# Revit family: FU_Modular_Sandler_Tetris 8100PT
name_source: partatom
category: Furniture
units: mm (PartAtom-declared; Revit-internal decimal feet)

## family parameters
Always vertical = Yes
Cut with Voids When Loaded = No
OmniClass Number = 23.40.20.00
OmniClass Title = General Furniture and Specialties
Render Appearance Source = Family Geometry
Room Calculation Point = No
Shared = No
Work Plane-Based = No

## types (1)
- Tetris 8100PT
    Default Elevation = 0 mm  [stored 0 ft]
    Depth = 850 mm  [stored 2.78871 ft]
    Description = Upholstered rear privacy screen for sofas and modules with backrest. Width 100cm / 39.4". To be used with the Tetris range.
    Height = 1300 mm  [stored 4.26509 ft]
    Manufacturer = Sandler
    Model = Tetris 8100PT
    URL = https://www.sandlerseating.com
    Width = 1100 mm

note: [stored X ft] marks values corroborated as IEEE doubles in the binary element streams (Revit-internal decimal feet)

## geometry (parser evidence)
native form markers: Sweep x5
no freeform markers — native parametric forms only
